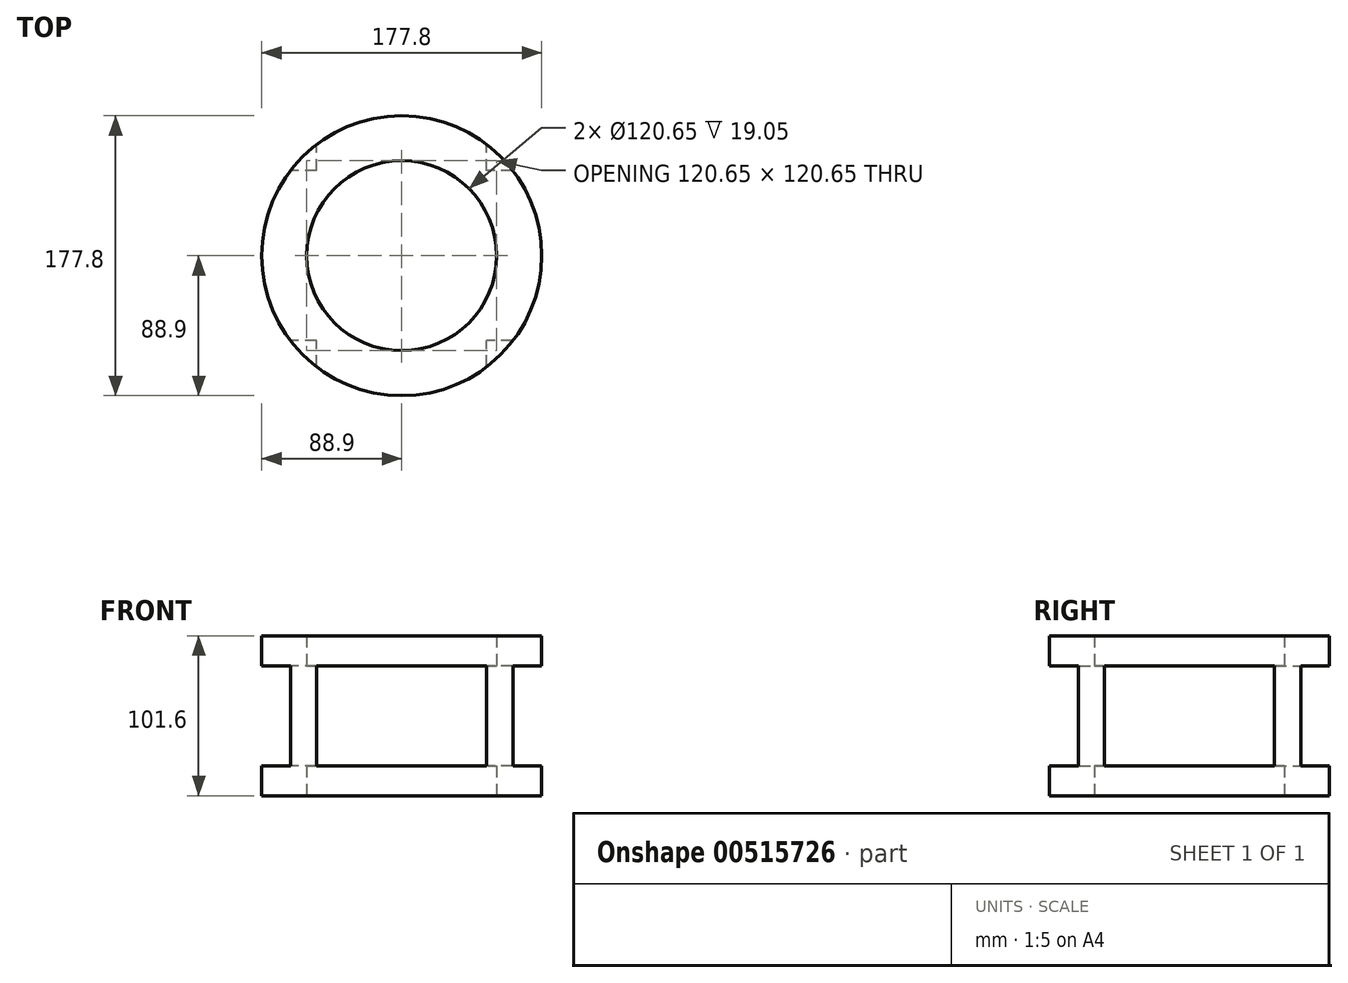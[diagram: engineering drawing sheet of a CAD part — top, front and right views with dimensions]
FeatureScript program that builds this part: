
annotation { "Feature Type Name" : "Feature", "Feature Type Description" : "" }
export const myFeature = defineFeature(function(context is Context, id is Id, definition is map)
    precondition{}
    {
        {
            var Q0;
            Q0=qCreatedBy(makeId("Top.planeOp"),FACE);
            var sketch = newSketch(context, id + "F0", { "sketchPlane" : qUnion([Q0])});
            skCircle(sketch, "E0", {"center": v(0, 0) * mm, "radius": 88.9 * mm});
            skSolve(sketch);
        }
        {
            var Q0;
            Q0 = qSketchRegion(id + "F0", true);
            extrude(context, id + "F1", {"entities" : qUnion([Q0]), "endBound" : BoundingType.SYMMETRIC, "depth" : 101.6 * mm, "offsetDistance" : 25.4 * mm});
        }
        {
            var Q0;
            Q0=qCreatedBy(makeId("Top.planeOp"),FACE);
            var sketch = newSketch(context, id + "F2", { "sketchPlane" : qUnion([Q0])});
            skCircle(sketch, "E1", {"center": v(0, 0) * mm, "radius": 60.33 * mm});
            skSolve(sketch);
        }
        {
            var Q0;
            Q0 = qSketchRegion(id + "F2", true);
            extrude(context, id + "F3", {"entities" : qUnion([Q0]), "operationType" : NewBodyOperationType.REMOVE, "endBound" : BoundingType.SYMMETRIC, "depth" : 104.14 * mm, "offsetDistance" : 25.4 * mm});
        }
        {
            var Q0;
            Q0=qCreatedBy(makeId("Front.planeOp"),FACE);
            var sketch = newSketch(context, id + "F4", { "sketchPlane" : qUnion([Q0])});
            skLineSegment(sketch, "E2.bottom", {"start": v(53.98, 31.75) * mm, "end": v(-53.98, 31.75) * mm});
            skLineSegment(sketch, "E2.top", {"start": v(53.98, -31.75) * mm, "end": v(-53.98, -31.75) * mm});
            skLineSegment(sketch, "E2.left", {"start": v(53.98, 31.75) * mm, "end": v(53.98, -31.75) * mm});
            skLineSegment(sketch, "E2.right", {"start": v(-53.98, 31.75) * mm, "end": v(-53.98, -31.75) * mm});
            skPoint(sketch, "E2.middle", {"position": v(0, 0) * mm});
            skSolve(sketch);
        }
        {
            var Q0;
            Q0 = qSketchRegion(id + "F4", true);
            extrude(context, id + "F5", {"entities" : qUnion([Q0]), "operationType" : NewBodyOperationType.REMOVE, "endBound" : BoundingType.SYMMETRIC, "depth" : 203.2 * mm, "offsetDistance" : 25.4 * mm});
        }
        {
            var Q0;
            Q0=qCreatedBy(makeId("Right.planeOp"),FACE);
            var sketch = newSketch(context, id + "F6", { "sketchPlane" : qUnion([Q0])});
            skLineSegment(sketch, "E3.bottom", {"start": v(53.98, 31.75) * mm, "end": v(-53.97, 31.75) * mm});
            skLineSegment(sketch, "E3.top", {"start": v(53.98, -31.75) * mm, "end": v(-53.97, -31.75) * mm});
            skLineSegment(sketch, "E3.left", {"start": v(53.98, 31.75) * mm, "end": v(53.98, -31.75) * mm});
            skLineSegment(sketch, "E3.right", {"start": v(-53.97, 31.75) * mm, "end": v(-53.97, -31.75) * mm});
            skPoint(sketch, "E3.middle", {"position": v(0, 0) * mm});
            skSolve(sketch);
        }
        {
            var Q0;
            Q0 = qSketchRegion(id + "F6", true);
            extrude(context, id + "F7", {"entities" : qUnion([Q0]), "operationType" : NewBodyOperationType.REMOVE, "endBound" : BoundingType.SYMMETRIC, "depth" : 203.2 * mm, "offsetDistance" : 25.4 * mm});
        }
    });
